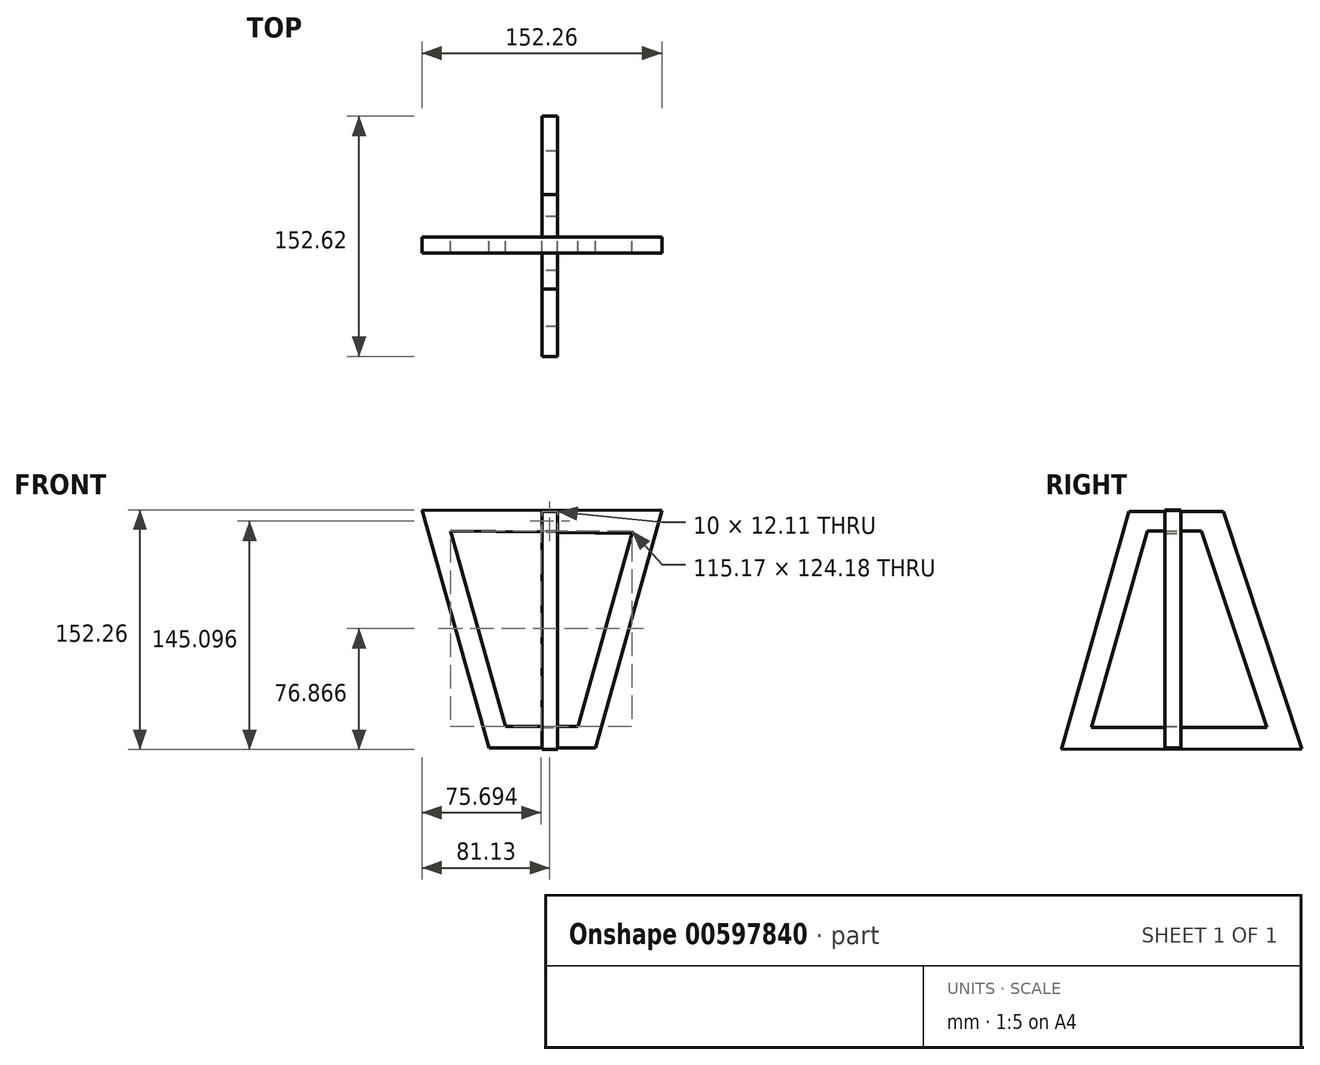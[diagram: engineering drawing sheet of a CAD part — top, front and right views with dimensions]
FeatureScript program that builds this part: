
annotation { "Feature Type Name" : "Feature", "Feature Type Description" : "" }
export const myFeature = defineFeature(function(context is Context, id is Id, definition is map)
    precondition{}
    {
        {
            var Q0;
            Q0=qCreatedBy(makeId("Front.planeOp"),FACE);
            var sketch = newSketch(context, id + "F0", { "sketchPlane" : qUnion([Q0])});
            skLineSegment(sketch, "E0", {"start": v(-76.13, 75.76) * mm, "end": v(-33.63, -75.39) * mm});
            skLineSegment(sketch, "E1", {"start": v(-33.63, -75.39) * mm, "end": v(34, -75.39) * mm});
            skLineSegment(sketch, "E2", {"start": v(34, -75.39) * mm, "end": v(76.13, 75.39) * mm});
            skLineSegment(sketch, "E3", {"start": v(76.13, 75.39) * mm, "end": v(-76.13, 75.76) * mm});
            skLineSegment(sketch, "E4", {"start": v(-58.02, 62.45) * mm, "end": v(-23.1, -61.72) * mm});
            skLineSegment(sketch, "E5", {"start": v(-23.1, -61.72) * mm, "end": v(22.91, -61.72) * mm});
            skLineSegment(sketch, "E6", {"start": v(22.91, -61.72) * mm, "end": v(57.15, 60.8) * mm});
            skLineSegment(sketch, "E7", {"start": v(57.15, 60.8) * mm, "end": v(-58.02, 62.45) * mm});
            skSolve(sketch);
        }
        {
            var Q0;
            Q0=makeQuery(id+"F0.imprint","IMPRINT",FACE,{"disambiguationData":[TD([[makeQuery(id+"F0.imprint","IMPRINT",EDGE,{"derivedFrom":sQuery(id+"F0.wireOp",EDGE,"E0")}),1.0]])]});
            extrude(context, id + "F1", {"entities" : qUnion([Q0]), "depth" : 10 * mm, "offsetDistance" : 25.4 * mm});
        }
        {
            var Q0;
            Q0=qCreatedBy(makeId("Right.planeOp"),FACE);
            var sketch = newSketch(context, id + "F2", { "sketchPlane" : qUnion([Q0])});
            skLineSegment(sketch, "E8", {"start": v(-75.76, -76.5) * mm, "end": v(-32.89, 74.65) * mm});
            skLineSegment(sketch, "E9", {"start": v(-32.89, 74.65) * mm, "end": v(26.98, 74.65) * mm});
            skLineSegment(sketch, "E10", {"start": v(26.98, 74.65) * mm, "end": v(76.86, -76.01) * mm});
            skLineSegment(sketch, "E11", {"start": v(76.86, -76.01) * mm, "end": v(-75.76, -76.5) * mm});
            skLineSegment(sketch, "E12", {"start": v(-56.66, -62.28) * mm, "end": v(-21.26, 62.54) * mm});
            skLineSegment(sketch, "E13", {"start": v(-21.26, 62.54) * mm, "end": v(13.21, 62.54) * mm});
            skLineSegment(sketch, "E14", {"start": v(13.21, 62.54) * mm, "end": v(51.92, -54.36) * mm});
            skPoint(sketch, "E14.endSnap0", {"position": v(51.92, -0.68) * mm});
            skLineSegment(sketch, "E15", {"start": v(51.92, -54.36) * mm, "end": v(54.54, -62.28) * mm});
            skLineSegment(sketch, "E16", {"start": v(54.54, -62.28) * mm, "end": v(-56.66, -62.28) * mm});
            skSolve(sketch);
        }
        {
            var Q0;
            Q0=makeQuery(id+"F2.imprint","IMPRINT",FACE,{"disambiguationData":[TD([[makeQuery(id+"F2.imprint","IMPRINT",EDGE,{"derivedFrom":sQuery(id+"F2.wireOp",EDGE,"E8")}),-1.0]])]});
            extrude(context, id + "F3", {"entities" : qUnion([Q0]), "operationType" : NewBodyOperationType.ADD, "depth" : 10 * mm, "offsetDistance" : 25.4 * mm});
        }
    });
